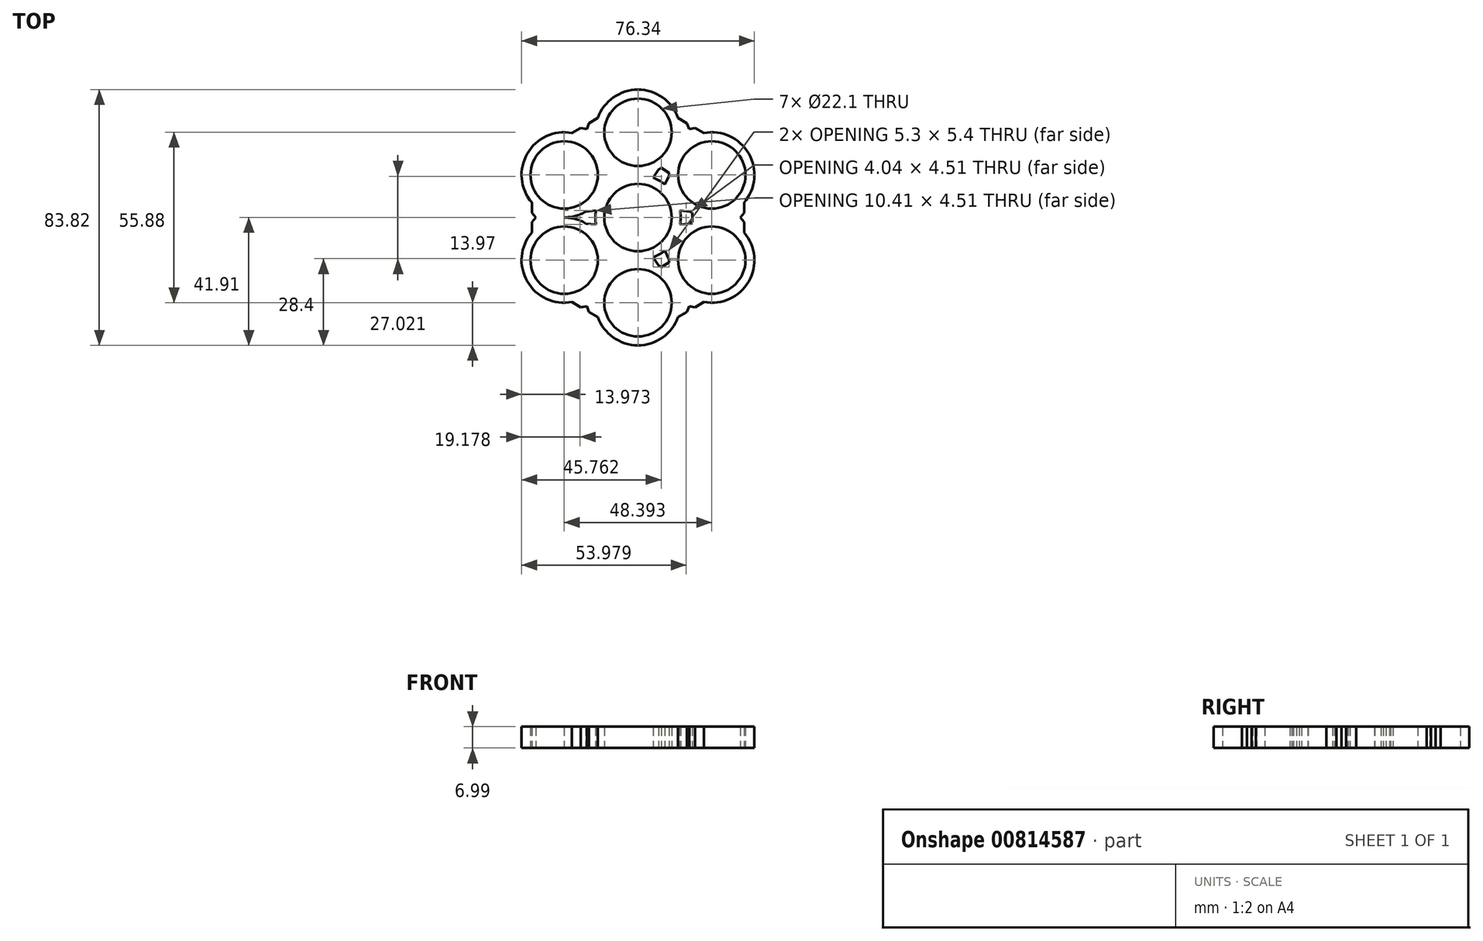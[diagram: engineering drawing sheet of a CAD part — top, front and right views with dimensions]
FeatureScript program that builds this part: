
annotation { "Feature Type Name" : "Feature", "Feature Type Description" : "" }
export const myFeature = defineFeature(function(context is Context, id is Id, definition is map)
    precondition{}
    {
        {
            var Q0;
            Q0=qCreatedBy(makeId("Top.planeOp"),FACE);
            var sketch = newSketch(context, id + "F0", { "sketchPlane" : qUnion([Q0])});
            skCircle(sketch, "E0", {"center": v(0, 0) * mm, "radius": 13.97 * mm});
            skCircle(sketch, "E1", {"center": v(0, 0) * mm, "radius": 11.05 * mm});
            skCircle(sketch, "E2", {"center": v(0, 27.94) * mm, "radius": 13.97 * mm});
            skCircle(sketch, "E3.1.0", {"center": v(-24.2, 13.97) * mm, "radius": 13.97 * mm});
            skCircle(sketch, "E3.2.0", {"center": v(-24.2, -13.97) * mm, "radius": 13.97 * mm});
            skCircle(sketch, "E3.3.0", {"center": v(0, -27.94) * mm, "radius": 13.97 * mm});
            skCircle(sketch, "E3.4.0", {"center": v(24.2, -13.97) * mm, "radius": 13.97 * mm});
            skCircle(sketch, "E3.5.0", {"center": v(24.2, 13.97) * mm, "radius": 13.97 * mm});
            skPoint(sketch, "E4", {"position": v(-13.16, 32.62) * mm});
            skPoint(sketch, "E5", {"position": v(13.16, 32.62) * mm});
            skPoint(sketch, "E6.1.1", {"position": v(-34.83, 4.91) * mm});
            skPoint(sketch, "E6.1.2", {"position": v(-21.67, 27.7) * mm});
            skPoint(sketch, "E6.2.1", {"position": v(-21.67, -27.7) * mm});
            skPoint(sketch, "E6.2.2", {"position": v(-34.83, -4.91) * mm});
            skPoint(sketch, "E6.3.1", {"position": v(13.16, -32.62) * mm});
            skPoint(sketch, "E6.3.2", {"position": v(-13.16, -32.62) * mm});
            skPoint(sketch, "E6.4.1", {"position": v(34.83, -4.91) * mm});
            skPoint(sketch, "E6.4.2", {"position": v(21.67, -27.7) * mm});
            skPoint(sketch, "E6.5.1", {"position": v(21.67, 27.7) * mm});
            skPoint(sketch, "E6.5.2", {"position": v(34.83, 4.91) * mm});
            skPoint(sketch, "E7", {"position": v(-10.23, 13.78) * mm});
            skPoint(sketch, "E8", {"position": v(-7.59, 16.2) * mm});
            skPoint(sketch, "E9", {"position": v(10.23, 13.78) * mm});
            skPoint(sketch, "E10", {"position": v(7.59, 16.2) * mm});
            skPoint(sketch, "E11.1.0", {"position": v(-17.05, -1.97) * mm});
            skPoint(sketch, "E11.1.1", {"position": v(-17.83, 1.53) * mm});
            skPoint(sketch, "E11.1.2", {"position": v(-10.24, 14.67) * mm});
            skPoint(sketch, "E11.1.3", {"position": v(-6.82, 15.75) * mm});
            skPoint(sketch, "E11.2.0", {"position": v(-6.82, -15.75) * mm});
            skPoint(sketch, "E11.2.1", {"position": v(-10.24, -14.67) * mm});
            skPoint(sketch, "E11.2.2", {"position": v(-17.83, -1.53) * mm});
            skPoint(sketch, "E11.2.3", {"position": v(-17.05, 1.97) * mm});
            skPoint(sketch, "E11.3.0", {"position": v(10.23, -13.78) * mm});
            skPoint(sketch, "E11.3.1", {"position": v(7.59, -16.2) * mm});
            skPoint(sketch, "E11.3.2", {"position": v(-7.59, -16.2) * mm});
            skPoint(sketch, "E11.3.3", {"position": v(-10.23, -13.78) * mm});
            skPoint(sketch, "E11.4.0", {"position": v(17.05, 1.97) * mm});
            skPoint(sketch, "E11.4.1", {"position": v(17.83, -1.53) * mm});
            skPoint(sketch, "E11.4.2", {"position": v(10.24, -14.67) * mm});
            skPoint(sketch, "E11.4.3", {"position": v(6.82, -15.75) * mm});
            skPoint(sketch, "E11.5.0", {"position": v(6.82, 15.75) * mm});
            skPoint(sketch, "E11.5.1", {"position": v(10.24, 14.67) * mm});
            skPoint(sketch, "E11.5.2", {"position": v(17.83, 1.53) * mm});
            skPoint(sketch, "E11.5.3", {"position": v(17.05, -1.97) * mm});
            skLineSegment(sketch, "E12", {"start": v(-7.59, 16.2) * mm, "end": v(-10.24, 14.67) * mm});
            skPoint(sketch, "E13", {"position": v(-8.85, 10.81) * mm});
            skPoint(sketch, "E14", {"position": v(8.85, 10.81) * mm});
            skPoint(sketch, "E15.1.3", {"position": v(-4.94, 13.07) * mm});
            skPoint(sketch, "E15.2.1", {"position": v(-8.94, -10.74) * mm});
            skPoint(sketch, "E15.2.2", {"position": v(-13.77, -2.37) * mm});
            skPoint(sketch, "E15.2.3", {"position": v(-13.79, 2.26) * mm});
            skPoint(sketch, "E15.3.0", {"position": v(8.85, -10.81) * mm});
            skPoint(sketch, "E15.3.1", {"position": v(4.83, -13.1) * mm});
            skPoint(sketch, "E15.3.2", {"position": v(-4.83, -13.1) * mm});
            skPoint(sketch, "E15.4.0", {"position": v(13.79, 2.26) * mm});
            skPoint(sketch, "E15.4.2", {"position": v(8.94, -10.74) * mm});
            skPoint(sketch, "E15.5.0", {"position": v(4.94, 13.07) * mm});
            skPoint(sketch, "E15.5.3", {"position": v(13.79, -2.26) * mm});
            skLineSegment(sketch, "E16", {"start": v(-10.23, 13.78) * mm, "end": v(-8.85, 10.81) * mm});
            skLineSegment(sketch, "E17", {"start": v(-6.82, 15.75) * mm, "end": v(-4.94, 13.07) * mm});
            skLineSegment(sketch, "E18", {"start": v(6.82, 15.75) * mm, "end": v(4.94, 13.07) * mm});
            skLineSegment(sketch, "E19", {"start": v(10.23, 13.78) * mm, "end": v(8.85, 10.81) * mm});
            skLineSegment(sketch, "E20.1.0", {"start": v(-6.82, -15.75) * mm, "end": v(-4.94, -13.07) * mm});
            skLineSegment(sketch, "E20.1.1", {"start": v(-10.23, -13.78) * mm, "end": v(-8.85, -10.81) * mm});
            skLineSegment(sketch, "E20.1.2", {"start": v(-17.05, -1.97) * mm, "end": v(-13.79, -2.26) * mm});
            skLineSegment(sketch, "E20.1.3", {"start": v(-17.05, 1.97) * mm, "end": v(-13.79, 2.26) * mm});
            skLineSegment(sketch, "E20.2.0", {"start": v(17.05, 1.97) * mm, "end": v(13.79, 2.26) * mm});
            skLineSegment(sketch, "E20.2.1", {"start": v(17.05, -1.97) * mm, "end": v(13.79, -2.26) * mm});
            skLineSegment(sketch, "E20.2.2", {"start": v(10.23, -13.78) * mm, "end": v(8.85, -10.81) * mm});
            skLineSegment(sketch, "E20.2.3", {"start": v(6.82, -15.75) * mm, "end": v(4.94, -13.07) * mm});
            skLineSegment(sketch, "E21", {"start": v(7.59, 16.2) * mm, "end": v(10.24, 14.67) * mm});
            skLineSegment(sketch, "E22.1.0", {"start": v(-10.24, -14.67) * mm, "end": v(-7.59, -16.2) * mm});
            skLineSegment(sketch, "E22.1.1", {"start": v(-17.83, -1.53) * mm, "end": v(-17.83, 1.53) * mm});
            skLineSegment(sketch, "E22.2.0", {"start": v(17.83, -1.53) * mm, "end": v(17.83, 1.53) * mm});
            skLineSegment(sketch, "E22.2.1", {"start": v(10.24, -14.67) * mm, "end": v(7.59, -16.2) * mm});
            skPoint(sketch, "E23", {"position": v(-34.83, 1.53) * mm});
            skPoint(sketch, "E24", {"position": v(-34.83, -1.53) * mm});
            skPoint(sketch, "E25", {"position": v(-33.5, 0) * mm});
            skPoint(sketch, "E26.1.0", {"position": v(-18.74, -29.4) * mm});
            skPoint(sketch, "E26.1.1", {"position": v(-16.75, -29.02) * mm});
            skPoint(sketch, "E26.1.2", {"position": v(-16.09, -30.93) * mm});
            skPoint(sketch, "E26.2.0", {"position": v(16.09, -30.93) * mm});
            skPoint(sketch, "E26.2.1", {"position": v(16.75, -29.02) * mm});
            skPoint(sketch, "E26.2.2", {"position": v(18.74, -29.4) * mm});
            skPoint(sketch, "E27.0.3.0", {"position": v(34.83, -1.53) * mm});
            skPoint(sketch, "E27.1.3.0", {"position": v(33.5, 0) * mm});
            skPoint(sketch, "E27.2.3.0", {"position": v(34.83, 1.53) * mm});
            skPoint(sketch, "E27.0.4.0", {"position": v(18.74, 29.4) * mm});
            skPoint(sketch, "E27.1.4.0", {"position": v(16.75, 29.02) * mm});
            skPoint(sketch, "E27.2.4.0", {"position": v(16.09, 30.93) * mm});
            skPoint(sketch, "E27.0.5.0", {"position": v(-16.09, 30.93) * mm});
            skPoint(sketch, "E27.1.5.0", {"position": v(-16.75, 29.02) * mm});
            skPoint(sketch, "E27.2.5.0", {"position": v(-18.74, 29.4) * mm});
            skLineSegment(sketch, "E28", {"start": v(-34.83, -1.53) * mm, "end": v(-33.5, 0) * mm});
            skLineSegment(sketch, "E29", {"start": v(-34.83, 1.53) * mm, "end": v(-33.5, 0) * mm});
            skLineSegment(sketch, "E30.1.0", {"start": v(-18.74, -29.4) * mm, "end": v(-16.75, -29.02) * mm});
            skLineSegment(sketch, "E30.1.1", {"start": v(-16.09, -30.93) * mm, "end": v(-16.75, -29.02) * mm});
            skLineSegment(sketch, "E30.2.0", {"start": v(16.09, -30.93) * mm, "end": v(16.75, -29.02) * mm});
            skLineSegment(sketch, "E30.2.1", {"start": v(18.74, -29.4) * mm, "end": v(16.75, -29.02) * mm});
            skLineSegment(sketch, "E30.3.0", {"start": v(34.83, -1.53) * mm, "end": v(33.5, 0) * mm});
            skLineSegment(sketch, "E30.3.1", {"start": v(34.83, 1.53) * mm, "end": v(33.5, 0) * mm});
            skLineSegment(sketch, "E30.4.0", {"start": v(18.74, 29.4) * mm, "end": v(16.75, 29.02) * mm});
            skLineSegment(sketch, "E30.4.1", {"start": v(16.09, 30.93) * mm, "end": v(16.75, 29.02) * mm});
            skLineSegment(sketch, "E30.5.0", {"start": v(-16.09, 30.93) * mm, "end": v(-16.75, 29.02) * mm});
            skLineSegment(sketch, "E30.5.1", {"start": v(-18.74, 29.4) * mm, "end": v(-16.75, 29.02) * mm});
            skLineSegment(sketch, "E31", {"start": v(-34.83, 4.91) * mm, "end": v(-34.83, 1.53) * mm});
            skLineSegment(sketch, "E32", {"start": v(-34.83, -1.53) * mm, "end": v(-34.83, -4.91) * mm});
            skLineSegment(sketch, "E33", {"start": v(-21.67, -27.7) * mm, "end": v(-18.74, -29.4) * mm});
            skLineSegment(sketch, "E34", {"start": v(-16.09, -30.93) * mm, "end": v(-13.16, -32.62) * mm});
            skLineSegment(sketch, "E35", {"start": v(13.16, -32.62) * mm, "end": v(16.09, -30.93) * mm});
            skLineSegment(sketch, "E36", {"start": v(18.74, -29.4) * mm, "end": v(21.67, -27.7) * mm});
            skLineSegment(sketch, "E37", {"start": v(34.83, -4.91) * mm, "end": v(34.83, -1.53) * mm});
            skLineSegment(sketch, "E38", {"start": v(34.83, 1.53) * mm, "end": v(34.83, 4.91) * mm});
            skLineSegment(sketch, "E39", {"start": v(21.67, 27.7) * mm, "end": v(18.74, 29.4) * mm});
            skLineSegment(sketch, "E40", {"start": v(16.09, 30.93) * mm, "end": v(13.16, 32.62) * mm});
            skLineSegment(sketch, "E41", {"start": v(-13.16, 32.62) * mm, "end": v(-16.09, 30.93) * mm});
            skLineSegment(sketch, "E42", {"start": v(-18.74, 29.4) * mm, "end": v(-21.67, 27.7) * mm});
            skCircle(sketch, "E43", {"center": v(0, 27.94) * mm, "radius": 11.05 * mm});
            skCircle(sketch, "E44.1.0", {"center": v(-24.2, -13.97) * mm, "radius": 11.05 * mm});
            skCircle(sketch, "E44.2.0", {"center": v(24.2, -13.97) * mm, "radius": 11.05 * mm});
            skCircle(sketch, "E45", {"center": v(-24.2, 13.97) * mm, "radius": 11.05 * mm});
            skCircle(sketch, "E46.1.0", {"center": v(0, -27.94) * mm, "radius": 11.05 * mm});
            skCircle(sketch, "E46.2.0", {"center": v(24.2, 13.97) * mm, "radius": 11.05 * mm});
            skSolve(sketch);
        }
        {
            var Q0;
            Q0=makeQuery(id+"F0.imprint","IMPRINT",FACE,{"disambiguationData":[TD([[makeQuery(id+"F0.imprint","IMPRINT",EDGE,{"derivedFrom":sQuery(id+"F0.wireOp",EDGE,"E3.1.0")}),-1.0]])]});
            var Q1;
            {var subQ0=sQuery(id+"F0.wireOp",EDGE,"E16");Q1=makeQuery(id+"F0.imprint","IMPRINT",FACE,{"disambiguationData":[TD([[makeQuery(id+"F0.imprint","IMPRINT",EDGE,{"derivedFrom":subQ0}),-1.0]])]});}
            var Q2;
            {var subQ0=sQuery(id+"F0.wireOp",EDGE,"E17");Q2=makeQuery(id+"F0.imprint","IMPRINT",FACE,{"disambiguationData":[TD([[makeQuery(id+"F0.imprint","IMPRINT",EDGE,{"derivedFrom":subQ0}),1.0]])]});}
            var Q3;
            Q3=makeQuery(id+"F0.imprint","IMPRINT",FACE,{"disambiguationData":[TD([[makeQuery(id+"F0.imprint","IMPRINT",EDGE,{"derivedFrom":sQuery(id+"F0.wireOp",EDGE,"E2")}),-1.0]])]});
            var Q4;
            {var subQ0=sQuery(id+"F0.wireOp",EDGE,"E18");Q4=makeQuery(id+"F0.imprint","IMPRINT",FACE,{"disambiguationData":[TD([[makeQuery(id+"F0.imprint","IMPRINT",EDGE,{"derivedFrom":subQ0}),-1.0]])]});}
            var Q5;
            {var subQ0=sQuery(id+"F0.wireOp",EDGE,"E19");Q5=makeQuery(id+"F0.imprint","IMPRINT",FACE,{"disambiguationData":[TD([[makeQuery(id+"F0.imprint","IMPRINT",EDGE,{"derivedFrom":subQ0}),1.0]])]});}
            var Q6;
            Q6=makeQuery(id+"F0.imprint","IMPRINT",FACE,{"disambiguationData":[TD([[makeQuery(id+"F0.imprint","IMPRINT",EDGE,{"derivedFrom":sQuery(id+"F0.wireOp",EDGE,"E3.5.0")}),-1.0]])]});
            var Q7;
            {var subQ0=sQuery(id+"F0.wireOp",EDGE,"E20.2.0");Q7=makeQuery(id+"F0.imprint","IMPRINT",FACE,{"disambiguationData":[TD([[makeQuery(id+"F0.imprint","IMPRINT",EDGE,{"derivedFrom":subQ0}),-1.0]])]});}
            var Q8;
            {var subQ0=sQuery(id+"F0.wireOp",EDGE,"E20.2.1");Q8=makeQuery(id+"F0.imprint","IMPRINT",FACE,{"disambiguationData":[TD([[makeQuery(id+"F0.imprint","IMPRINT",EDGE,{"derivedFrom":subQ0}),1.0]])]});}
            var Q9;
            Q9=makeQuery(id+"F0.imprint","IMPRINT",FACE,{"disambiguationData":[TD([[makeQuery(id+"F0.imprint","IMPRINT",EDGE,{"derivedFrom":sQuery(id+"F0.wireOp",EDGE,"E3.4.0")}),-1.0]])]});
            var Q10;
            {var subQ0=sQuery(id+"F0.wireOp",EDGE,"E20.2.2");Q10=makeQuery(id+"F0.imprint","IMPRINT",FACE,{"disambiguationData":[TD([[makeQuery(id+"F0.imprint","IMPRINT",EDGE,{"derivedFrom":subQ0}),-1.0]])]});}
            var Q11;
            {var subQ0=sQuery(id+"F0.wireOp",EDGE,"E20.2.3");Q11=makeQuery(id+"F0.imprint","IMPRINT",FACE,{"disambiguationData":[TD([[makeQuery(id+"F0.imprint","IMPRINT",EDGE,{"derivedFrom":subQ0}),1.0]])]});}
            var Q12;
            Q12=makeQuery(id+"F0.imprint","IMPRINT",FACE,{"disambiguationData":[TD([[makeQuery(id+"F0.imprint","IMPRINT",EDGE,{"derivedFrom":sQuery(id+"F0.wireOp",EDGE,"E3.3.0")}),-1.0]])]});
            var Q13;
            {var subQ0=sQuery(id+"F0.wireOp",EDGE,"E20.1.0");Q13=makeQuery(id+"F0.imprint","IMPRINT",FACE,{"disambiguationData":[TD([[makeQuery(id+"F0.imprint","IMPRINT",EDGE,{"derivedFrom":subQ0}),-1.0]])]});}
            var Q14;
            Q14=makeQuery(id+"F0.imprint","IMPRINT",FACE,{"disambiguationData":[TD([[makeQuery(id+"F0.imprint","IMPRINT",EDGE,{"derivedFrom":sQuery(id+"F0.wireOp",EDGE,"E3.2.0")}),-1.0]])]});
            var Q15;
            {var subQ0=sQuery(id+"F0.wireOp",EDGE,"E20.1.1");Q15=makeQuery(id+"F0.imprint","IMPRINT",FACE,{"disambiguationData":[TD([[makeQuery(id+"F0.imprint","IMPRINT",EDGE,{"derivedFrom":subQ0}),1.0]])]});}
            var Q16;
            {var subQ0=sQuery(id+"F0.wireOp",EDGE,"E20.1.2");Q16=makeQuery(id+"F0.imprint","IMPRINT",FACE,{"disambiguationData":[TD([[makeQuery(id+"F0.imprint","IMPRINT",EDGE,{"derivedFrom":subQ0}),-1.0]])]});}
            var Q17;
            {var subQ0=sQuery(id+"F0.wireOp",EDGE,"E20.1.3");Q17=makeQuery(id+"F0.imprint","IMPRINT",FACE,{"disambiguationData":[TD([[makeQuery(id+"F0.imprint","IMPRINT",EDGE,{"derivedFrom":subQ0}),1.0]])]});}
            var Q18;
            {var subQ0=sQuery(id+"F0.wireOp",EDGE,"LLqchw5J-o6dg-3V9w-LCXr-S6bbMErBjwSO");Q18=makeQuery(id+"F0.imprint","IMPRINT",FACE,{"disambiguationData":[TD([[makeQuery(id+"F0.imprint","IMPRINT",EDGE,{"derivedFrom":subQ0}),1.0]])]});}
            var Q19;
            {var subQ0=sQuery(id+"F0.wireOp",EDGE,"LQmuZcvo-VVAQ-kA1a-CYmi-eegfPORy8C1y");Q19=makeQuery(id+"F0.imprint","IMPRINT",FACE,{"disambiguationData":[TD([[makeQuery(id+"F0.imprint","IMPRINT",EDGE,{"derivedFrom":subQ0}),1.0]])]});}
            var Q20;
            {var subQ0=sQuery(id+"F0.wireOp",EDGE,"iKP7NnxG-b0vM-gLNq-ULok-bc8D2REZiUFf");Q20=makeQuery(id+"F0.imprint","IMPRINT",FACE,{"disambiguationData":[TD([[makeQuery(id+"F0.imprint","IMPRINT",EDGE,{"derivedFrom":subQ0}),-1.0]])]});}
            var Q21;
            {var subQ0=sQuery(id+"F0.wireOp",EDGE,"g1o3A35l-0LKY-l3Zn-tp8K-zV1UiBWhMKCo");Q21=makeQuery(id+"F0.imprint","IMPRINT",FACE,{"disambiguationData":[TD([[makeQuery(id+"F0.imprint","IMPRINT",EDGE,{"derivedFrom":subQ0}),1.0]])]});}
            var Q22;
            {var subQ0=sQuery(id+"F0.wireOp",EDGE,"IokRFuHU-XKv6-MIJh-pz2j-d3q8Gzxv2vaR");Q22=makeQuery(id+"F0.imprint","IMPRINT",FACE,{"disambiguationData":[TD([[makeQuery(id+"F0.imprint","IMPRINT",EDGE,{"derivedFrom":subQ0}),-1.0]])]});}
            var Q23;
            Q23=makeQuery(id+"F0.imprint","IMPRINT",FACE,{"disambiguationData":[TD([[makeQuery(id+"F0.imprint","IMPRINT",EDGE,{"derivedFrom":sQuery(id+"F0.wireOp",EDGE,"E1")}),-1.0]])]});
            var Q24;
            {var subQ0=sQuery(id+"F0.wireOp",EDGE,"XQw3NFbb-Hulp-mxvm-6Yrm-zP847iwQHagt");Q24=makeQuery(id+"F0.imprint","IMPRINT",FACE,{"disambiguationData":[TD([[makeQuery(id+"F0.imprint","IMPRINT",EDGE,{"derivedFrom":subQ0}),1.0]])]});}
            var Q25;
            Q25=makeQuery(id+"F0.imprint","IMPRINT",FACE,{"disambiguationData":[TD([[makeQuery(id+"F0.imprint","IMPRINT",EDGE,{"derivedFrom":sQuery(id+"F0.wireOp",EDGE,"E28")}),-1.0]])]});
            var Q26;
            Q26=makeQuery(id+"F0.imprint","IMPRINT",FACE,{"disambiguationData":[TD([[makeQuery(id+"F0.imprint","IMPRINT",EDGE,{"derivedFrom":sQuery(id+"F0.wireOp",EDGE,"E30.5.0")}),1.0]])]});
            var Q27;
            Q27=makeQuery(id+"F0.imprint","IMPRINT",FACE,{"disambiguationData":[TD([[makeQuery(id+"F0.imprint","IMPRINT",EDGE,{"derivedFrom":sQuery(id+"F0.wireOp",EDGE,"E30.4.0")}),1.0]])]});
            var Q28;
            Q28=makeQuery(id+"F0.imprint","IMPRINT",FACE,{"disambiguationData":[TD([[makeQuery(id+"F0.imprint","IMPRINT",EDGE,{"derivedFrom":sQuery(id+"F0.wireOp",EDGE,"E30.3.0")}),1.0]])]});
            var Q29;
            Q29=makeQuery(id+"F0.imprint","IMPRINT",FACE,{"disambiguationData":[TD([[makeQuery(id+"F0.imprint","IMPRINT",EDGE,{"derivedFrom":sQuery(id+"F0.wireOp",EDGE,"E30.2.0")}),1.0]])]});
            var Q30;
            Q30=makeQuery(id+"F0.imprint","IMPRINT",FACE,{"disambiguationData":[TD([[makeQuery(id+"F0.imprint","IMPRINT",EDGE,{"derivedFrom":sQuery(id+"F0.wireOp",EDGE,"E30.1.0")}),1.0]])]});
            var Q31;
            Q31=makeQuery(id+"F0.imprint","IMPRINT",FACE,{"disambiguationData":[TD([[makeQuery(id+"F0.imprint","IMPRINT",EDGE,{"derivedFrom":sQuery(id+"F0.wireOp",EDGE,"E43")}),-1.0]])]});
            var Q32;
            Q32=makeQuery(id+"F0.imprint","IMPRINT",FACE,{"disambiguationData":[TD([[makeQuery(id+"F0.imprint","IMPRINT",EDGE,{"derivedFrom":sQuery(id+"F0.wireOp",EDGE,"E45")}),-1.0]])]});
            var Q33;
            Q33=makeQuery(id+"F0.imprint","IMPRINT",FACE,{"disambiguationData":[TD([[makeQuery(id+"F0.imprint","IMPRINT",EDGE,{"derivedFrom":sQuery(id+"F0.wireOp",EDGE,"E44.1.0")}),-1.0]])]});
            var Q34;
            Q34=makeQuery(id+"F0.imprint","IMPRINT",FACE,{"disambiguationData":[TD([[makeQuery(id+"F0.imprint","IMPRINT",EDGE,{"derivedFrom":sQuery(id+"F0.wireOp",EDGE,"E46.1.0")}),-1.0]])]});
            var Q35;
            Q35=makeQuery(id+"F0.imprint","IMPRINT",FACE,{"disambiguationData":[TD([[makeQuery(id+"F0.imprint","IMPRINT",EDGE,{"derivedFrom":sQuery(id+"F0.wireOp",EDGE,"E44.2.0")}),-1.0]])]});
            var Q36;
            Q36=makeQuery(id+"F0.imprint","IMPRINT",FACE,{"disambiguationData":[TD([[makeQuery(id+"F0.imprint","IMPRINT",EDGE,{"derivedFrom":sQuery(id+"F0.wireOp",EDGE,"E46.2.0")}),-1.0]])]});
            extrude(context, id + "F1", {"entities" : qUnion([Q0, Q1, Q2, Q3, Q4, Q5, Q6, Q7, Q8, Q9, Q10, Q11, Q12, Q13, Q14, Q15, Q16, Q17, Q18, Q19, Q20, Q21, Q22, Q23, Q24, Q25, Q26, Q27, Q28, Q29, Q30, Q31, Q32, Q33, Q34, Q35, Q36]), "depth" : 7 * mm, "offsetDistance" : 25.4 * mm});
        }
    });
